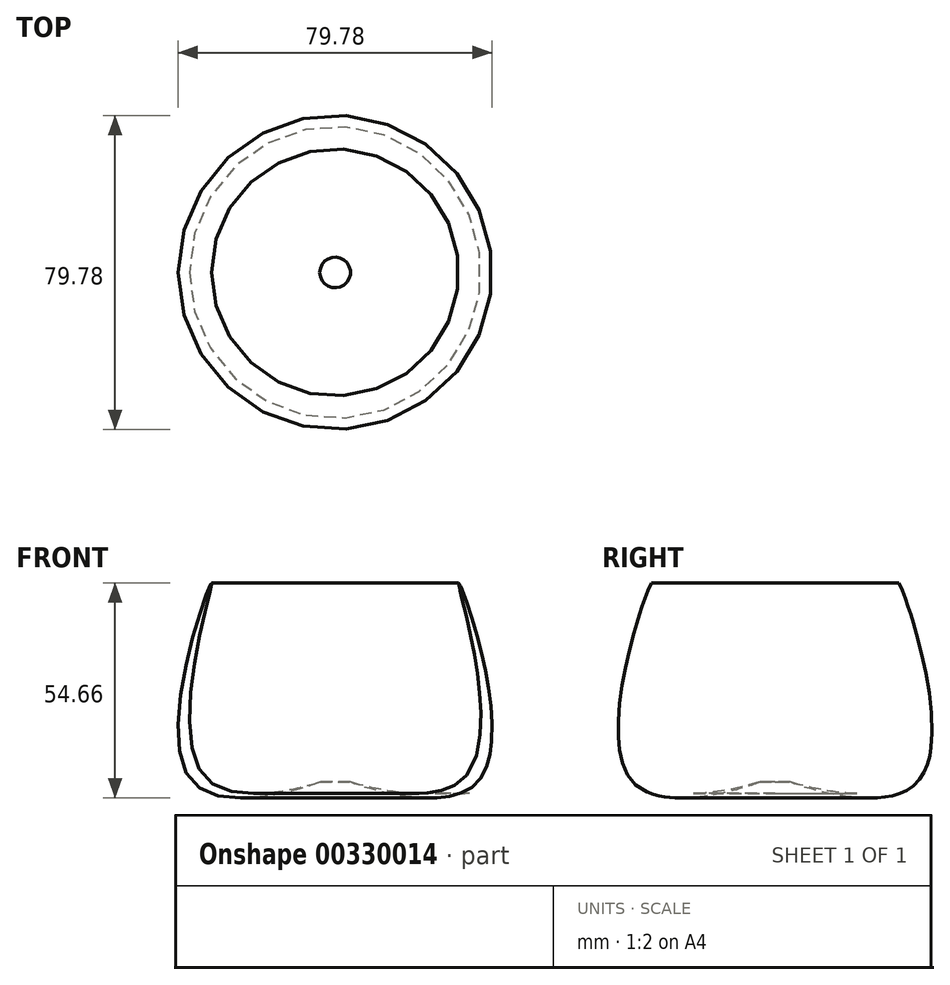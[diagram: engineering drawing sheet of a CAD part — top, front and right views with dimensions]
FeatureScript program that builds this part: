
annotation { "Feature Type Name" : "Feature", "Feature Type Description" : "" }
export const myFeature = defineFeature(function(context is Context, id is Id, definition is map)
    precondition{}
    {
        {
            var Q0;
            Q0=qCreatedBy(makeId("Top.planeOp"),FACE);
            var sketch = newSketch(context, id + "F0", { "sketchPlane" : qUnion([Q0])});
            skCircle(sketch, "E0", {"center": v(0, 0) * mm, "radius": 38.1 * mm});
            skCircle(sketch, "E1", {"center": v(0, 0) * mm, "radius": 3.81 * mm});
            skSolve(sketch);
        }
        {
            var Q0;
            Q0=sQuery(id+"F0.wireOp",EDGE,"E1");
            extrude(context, id + "F1", {"bodyType" : ToolBodyType.SURFACE, "surfaceEntities" : qUnion([Q0]), "depth" : 92.7 * mm});
        }
        {
            var Q0;
            Q0=sQuery(id+"F0.wireOp",EDGE,"E0");
            extrude(context, id + "F2", {"bodyType" : ToolBodyType.SURFACE, "surfaceEntities" : qUnion([Q0]), "depth" : 1.27 * mm});
        }
        {
            var Q0;
            Q0=qCreatedBy(makeId("Front.planeOp"),FACE);
            var sketch = newSketch(context, id + "F3", { "sketchPlane" : qUnion([Q0])});
            skFitSpline(sketch, "E2", {"points": [v(-3.9, 92.95) * mm, v(-36.18, 92.95) * mm, v(-31.4, 143.57) * mm, v(-32.99, 94.15) * mm, v(-3.9, 92.95) * mm]});
            skLineSegment(sketch, "E3", {"start": v(0, 114.87) * mm, "end": v(0, 93.35) * mm, "construction": true});
            skSolve(sketch);
        }
        {
            var Q0;
            Q0 = qSketchRegion(id + "F3", true);
            var Q1;
            Q1=sQuery(id+"F3.wireOp",EDGE,"E3");
            revolve(context, id + "F4", {"entities" : qUnion([Q0]), "axis" : qUnion([Q1]), "revolveType" : RevolveType.FULL});
        }
    });
